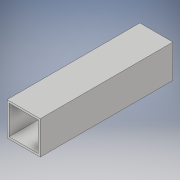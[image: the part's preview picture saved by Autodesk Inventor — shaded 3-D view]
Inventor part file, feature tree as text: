
AUTODESK INVENTOR PART (.ipt)
format: ipt  version: 2019 (Build 230136000, 136)  size: 94,720 bytes
history: native  units: in
note: dims shown in document units (in); Inventor stores cm internally (conversion verified against a paired STEP export)
features: extrude x1, sketch x1
ambient origin geometry x8: Origin, YZ Plane, XZ Plane, XY Plane, X Axis, Y Axis, Z Axis, Center Point
bodies: Solid1 (feature_tree)
feature tree (2):
  extrude  "Extrusion1"  Depth=2.0in
  sketch  "Sketch1"  dims[d0=2.0in d1=2.0in d2=0.125in d3=8.0in d4=0.0in]
